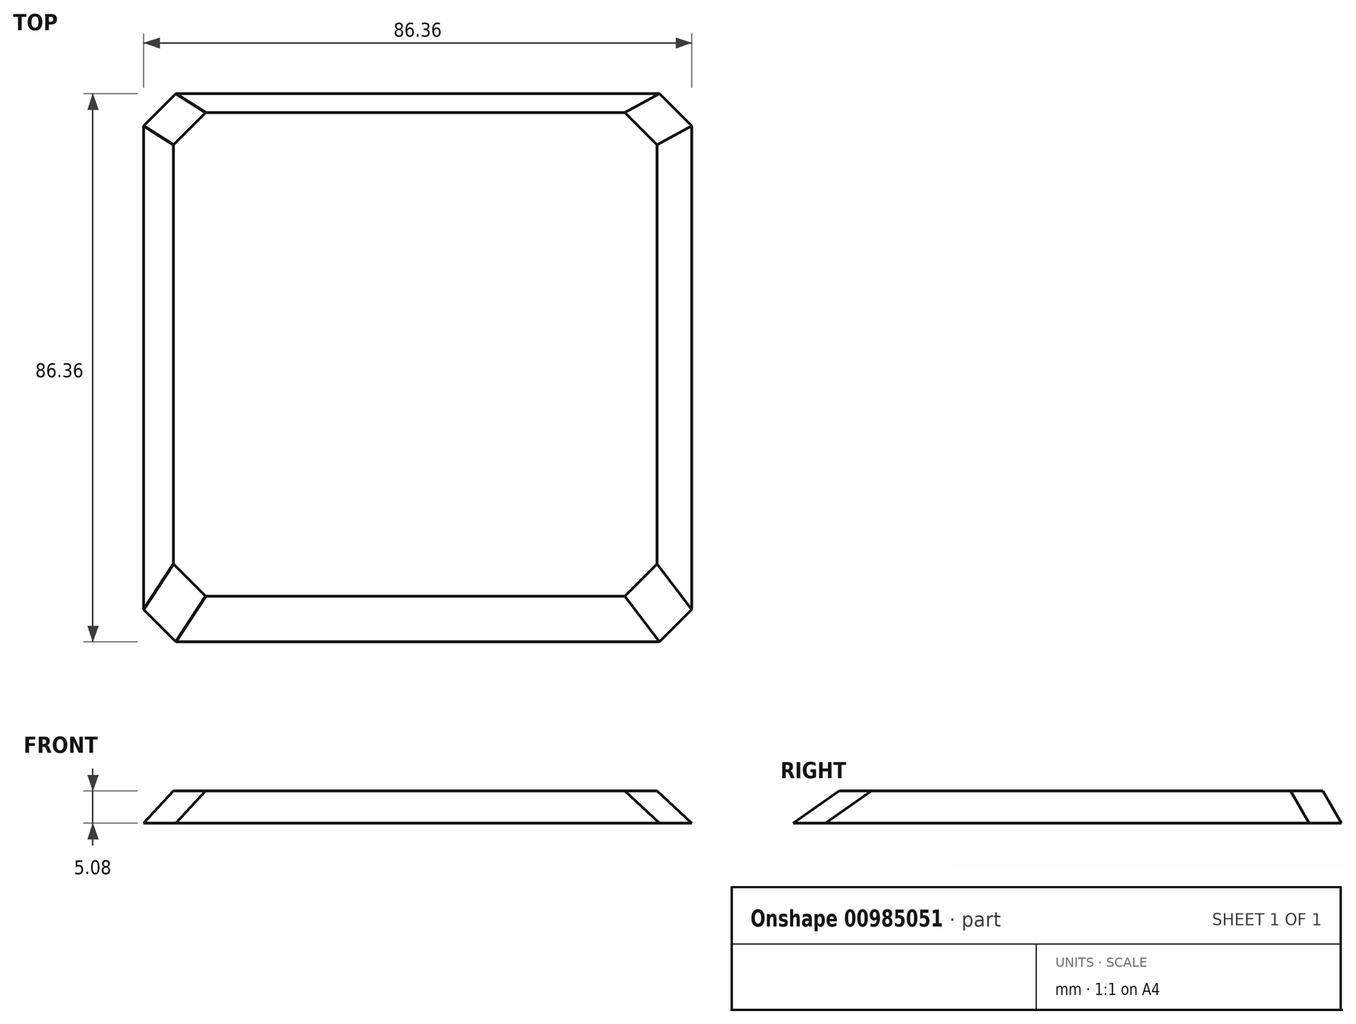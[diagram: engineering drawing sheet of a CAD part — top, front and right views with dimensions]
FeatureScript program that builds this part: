
annotation { "Feature Type Name" : "Feature", "Feature Type Description" : "" }
export const myFeature = defineFeature(function(context is Context, id is Id, definition is map)
    precondition{}
    {
        {
            var Q0;
            Q0=qCreatedBy(makeId("Top.planeOp"),FACE);
            var sketch = newSketch(context, id + "F0", { "sketchPlane" : qUnion([Q0])});
            skPoint(sketch, "E0.middle", {"position": v(0, 0) * mm});
            skLineSegment(sketch, "E1", {"start": v(-38.1, 43.18) * mm, "end": v(-43.18, 38.1) * mm});
            skLineSegment(sketch, "E2.MirrorCS", {"start": v(38.1, 43.18) * mm, "end": v(43.18, 38.1) * mm});
            skLineSegment(sketch, "E3.MirrorCS", {"start": v(-38.1, -43.18) * mm, "end": v(-43.18, -38.1) * mm});
            skLineSegment(sketch, "E4.MirrorCS", {"start": v(38.1, -43.18) * mm, "end": v(43.18, -38.1) * mm});
            skLineSegment(sketch, "E5", {"start": v(43.18, -38.1) * mm, "end": v(43.18, 38.1) * mm});
            skLineSegment(sketch, "E6", {"start": v(38.1, 43.18) * mm, "end": v(-38.1, 43.18) * mm});
            skLineSegment(sketch, "E7", {"start": v(-43.18, 38.1) * mm, "end": v(-43.18, -38.1) * mm});
            skLineSegment(sketch, "E8", {"start": v(-38.1, -43.18) * mm, "end": v(38.1, -43.18) * mm});
            skSolve(sketch);
        }
        {
            var Q0;
            Q0=makeQuery(id+"F0.imprint","IMPRINT",FACE,{"disambiguationData":[TD([[makeQuery(id+"F0.imprint","IMPRINT",EDGE,{"derivedFrom":sQuery(id+"F0.wireOp",EDGE,"E1")}),1.0]])]});
            cPlane(context, id + "F1", {"entities" : qUnion([Q0]), "cplaneType" : CPlaneType.OFFSET, "offset" : 5.08 * mm, "width" : 152.4 * mm, "height" : 152.4 * mm});
        }
        {
            var Q0;
            Q0=qCreatedBy(id+"F1.planeOp",FACE);
            var sketch = newSketch(context, id + "F2", { "sketchPlane" : qUnion([Q0])});
            skPoint(sketch, "E9.middle", {"position": v(-0.41, 2.13) * mm});
            skLineSegment(sketch, "E10", {"start": v(-38.51, 35.15) * mm, "end": v(-33.43, 40.23) * mm});
            skLineSegment(sketch, "E11.MirrorCS", {"start": v(37.69, 35.15) * mm, "end": v(32.6, 40.23) * mm});
            skLineSegment(sketch, "E12.MirrorCS", {"start": v(-38.51, -30.89) * mm, "end": v(-33.43, -35.97) * mm});
            skLineSegment(sketch, "E13.MirrorCS", {"start": v(37.69, -30.89) * mm, "end": v(32.6, -35.97) * mm});
            skLineSegment(sketch, "E14", {"start": v(37.69, -30.89) * mm, "end": v(37.69, 35.15) * mm});
            skLineSegment(sketch, "E15", {"start": v(32.6, 40.23) * mm, "end": v(-33.43, 40.23) * mm});
            skLineSegment(sketch, "E16", {"start": v(-38.51, 35.15) * mm, "end": v(-38.51, -30.89) * mm});
            skLineSegment(sketch, "E17", {"start": v(-33.43, -35.97) * mm, "end": v(32.6, -35.97) * mm});
            skSolve(sketch);
        }
        {
            var Q0;
            Q0=makeQuery(id+"F0.imprint","IMPRINT",FACE,{"disambiguationData":[TD([[makeQuery(id+"F0.imprint","IMPRINT",EDGE,{"derivedFrom":sQuery(id+"F0.wireOp",EDGE,"E1")}),1.0]])]});
            var Q1;
            Q1=makeQuery(id+"F2.imprint","IMPRINT",FACE,{"disambiguationData":[TD([[makeQuery(id+"F2.imprint","IMPRINT",EDGE,{"derivedFrom":sQuery(id+"F2.wireOp",EDGE,"E10")}),-1.0]])]});
            loft(context, id + "F3", {"sheetProfilesArray" : [{ "sheetProfileEntities" : qUnion([Q0]) }, { "sheetProfileEntities" : qUnion([Q1]) }]});
        }
    });
